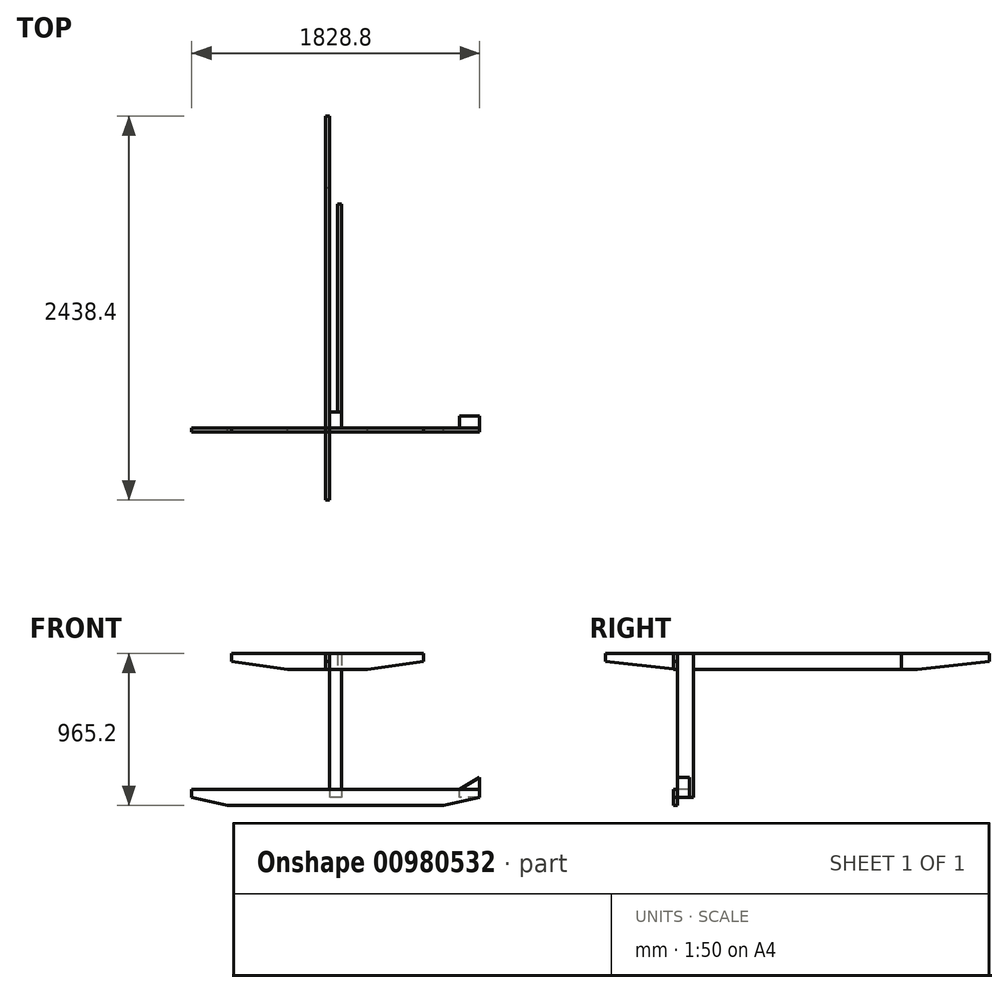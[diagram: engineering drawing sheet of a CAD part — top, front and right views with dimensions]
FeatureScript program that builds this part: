
annotation { "Feature Type Name" : "Feature", "Feature Type Description" : "" }
export const myFeature = defineFeature(function(context is Context, id is Id, definition is map)
    precondition{}
    {
        {
            var Q0;
            Q0=qCreatedBy(makeId("Right.planeOp"),FACE);
            var sketch = newSketch(context, id + "F0", { "sketchPlane" : qUnion([Q0])});
            skLineSegment(sketch, "E0.bottom", {"start": v(-1219.2, 50.8) * mm, "end": v(1219.2, 50.8) * mm});
            skLineSegment(sketch, "E0.left", {"start": v(-1219.2, 50.8) * mm, "end": v(-1219.2, 0) * mm});
            skLineSegment(sketch, "E0.right", {"start": v(1219.2, 50.8) * mm, "end": v(1219.2, 0) * mm});
            skLineSegment(sketch, "E1", {"start": v(-1219.2, -50.8) * mm, "end": v(1219.2, 50.8) * mm, "construction": true});
            skLineSegment(sketch, "E2", {"start": v(-1219.2, 0) * mm, "end": v(-762, -50.8) * mm});
            skLineSegment(sketch, "E3.MirrorCS", {"start": v(1219.2, 0) * mm, "end": v(762, -50.8) * mm});
            skLineSegment(sketch, "E4", {"start": v(762.5, -50.75) * mm, "end": v(762, -50.8) * mm});
            skLineSegment(sketch, "E5", {"start": v(-1219.2, 0) * mm, "end": v(-1219.2, -50.8) * mm});
            skLineSegment(sketch, "E6", {"start": v(-762, -50.8) * mm, "end": v(762, -50.8) * mm});
            skSolve(sketch);
        }
        {
            var Q0;
            Q0 = qSketchRegion(id + "F0", true);
            extrude(context, id + "F1", {"entities" : qUnion([Q0]), "endBound" : BoundingType.SYMMETRIC, "depth" : 25.4 * mm, "offsetDistance" : 25.4 * mm});
        }
        {
            var Q0;
            Q0=makeQuery(id+"F1.opExtrude","CAP_FACE",FACE,{"disambiguationData":[OSD([sQuery(id+"F0.wireOp",EDGE,"E0.bottom"),sQuery(id+"F0.wireOp",EDGE,"E0.left"),sQuery(id+"F0.wireOp",EDGE,"E0.right"),sQuery(id+"F0.wireOp",EDGE,"E2"),sQuery(id+"F0.wireOp",EDGE,"E3.MirrorCS"),sQuery(id+"F0.wireOp",EDGE,"E4"),sQuery(id+"F0.wireOp",EDGE,"E6")])],"isStart":false});
            var sketch = newSketch(context, id + "F2", { "sketchPlane" : qUnion([Q0])});
            skPoint(sketch, "E7", {"position": v(-762, 50.8) * mm});
            skLineSegment(sketch, "E8.bottom", {"start": v(-762, 50.8) * mm, "end": v(-660.4, 50.8) * mm});
            skLineSegment(sketch, "E8.top", {"start": v(-762, -863.6) * mm, "end": v(-660.4, -863.6) * mm});
            skLineSegment(sketch, "E8.left", {"start": v(-762, 50.8) * mm, "end": v(-762, -863.6) * mm});
            skLineSegment(sketch, "E8.right", {"start": v(-660.4, 50.8) * mm, "end": v(-660.4, -863.6) * mm});
            skSolve(sketch);
        }
        {
            var Q0;
            Q0 = qSketchRegion(id + "F2", true);
            extrude(context, id + "F3", {"entities" : qUnion([Q0]), "depth" : 76.2 * mm, "offsetDistance" : 25.4 * mm});
        }
        {
            var Q0;
            Q0=makeQuery(id+"F3.opExtrude","SWEPT_BODY",BODY,{"disambiguationData":[OSD([sQuery(id+"F2.wireOp",EDGE,"E8.bottom"),sQuery(id+"F2.wireOp",EDGE,"E8.top"),sQuery(id+"F2.wireOp",EDGE,"E8.left"),sQuery(id+"F2.wireOp",EDGE,"E8.right")])]});
            transform(context, id + "F4", {"entities" : qUnion([Q0]), "transformType" : TransformType.TRANSLATION_3D, "dx" : 0 * mm, "dy" : 1422.4 * mm, "dz" : 0 * mm, "makeCopy" : true});
        }
        {
            var Q0;
            Q0=makeQuery(id+"F3.opExtrude","SWEPT_FACE",FACE,{"disambiguationData":[OSD([sQuery(id+"F2.wireOp",EDGE,"E8.left")])]});
            var sketch = newSketch(context, id + "F5", { "sketchPlane" : qUnion([Q0])});
            skLineSegment(sketch, "E9.bottom", {"start": v(-609.6, 50.8) * mm, "end": v(609.6, 50.8) * mm});
            skLineSegment(sketch, "E9.top", {"start": v(-254, -50.8) * mm, "end": v(254, -50.8) * mm});
            skLineSegment(sketch, "E9.left", {"start": v(-609.6, 50.8) * mm, "end": v(-609.6, 0) * mm});
            skLineSegment(sketch, "E9.right", {"start": v(609.6, 50.8) * mm, "end": v(609.6, 0) * mm});
            skLineSegment(sketch, "E10", {"start": v(-609.6, 50.8) * mm, "end": v(609.6, -50.8) * mm, "construction": true});
            skLineSegment(sketch, "E11", {"start": v(-609.6, 0) * mm, "end": v(-254, -50.8) * mm});
            skPoint(sketch, "E12.orphan", {"position": v(-609.6, -50.8) * mm});
            skLineSegment(sketch, "E13.MirrorCS", {"start": v(609.6, 0) * mm, "end": v(254, -50.8) * mm});
            skSolve(sketch);
        }
        {
            var Q0;
            Q0 = qSketchRegion(id + "F5", true);
            extrude(context, id + "F6", {"entities" : qUnion([Q0]), "depth" : 25.4 * mm, "offsetDistance" : 25.4 * mm});
        }
        {
            var Q0;
            Q0=makeQuery(id+"F4.opPattern","COPY",BODY,{"derivedFrom":makeQuery(id+"F3.opExtrude","SWEPT_BODY",BODY,{"disambiguationData":[OSD([sQuery(id+"F2.wireOp",EDGE,"E8.bottom"),sQuery(id+"F2.wireOp",EDGE,"E8.top"),sQuery(id+"F2.wireOp",EDGE,"E8.left"),sQuery(id+"F2.wireOp",EDGE,"E8.right")])]}),"instanceName":"1"});
            deleteBodies(context, id + "F7", {"entities" : qUnion([Q0])});
        }
        {
            var Q0;
            Q0=makeQuery(id+"F3.opExtrude","SWEPT_FACE",FACE,{"disambiguationData":[OSD([sQuery(id+"F2.wireOp",EDGE,"E8.left")])]});
            var sketch = newSketch(context, id + "F8", { "sketchPlane" : qUnion([Q0])});
            skLineSegment(sketch, "E14.bottom", {"start": v(-863.6, -812.8) * mm, "end": v(965.2, -812.8) * mm});
            skLineSegment(sketch, "E14.top", {"start": v(-635, -914.4) * mm, "end": v(736.6, -914.4) * mm});
            skLineSegment(sketch, "E14.left", {"start": v(-863.6, -812.8) * mm, "end": v(-863.6, -863.6) * mm});
            skLineSegment(sketch, "E14.right", {"start": v(965.2, -812.8) * mm, "end": v(965.2, -863.6) * mm});
            skLineSegment(sketch, "E15", {"start": v(-863.6, -812.8) * mm, "end": v(965.2, -914.4) * mm, "construction": true});
            skLineSegment(sketch, "E16", {"start": v(-863.6, -863.6) * mm, "end": v(-635, -914.4) * mm});
            skPoint(sketch, "E17.orphan", {"position": v(-863.6, -914.4) * mm});
            skLineSegment(sketch, "E18.MirrorCS", {"start": v(965.2, -863.6) * mm, "end": v(736.6, -914.4) * mm});
            skSolve(sketch);
        }
        {
            var Q0;
            Q0 = qSketchRegion(id + "F8", true);
            extrude(context, id + "F9", {"entities" : qUnion([Q0]), "depth" : 25.4 * mm, "offsetDistance" : 25.4 * mm});
        }
        {
            var Q0;
            Q0=makeQuery(id+"F3.opExtrude","SWEPT_FACE",FACE,{"disambiguationData":[OSD([sQuery(id+"F2.wireOp",EDGE,"E8.right")])]});
            var sketch = newSketch(context, id + "F10", { "sketchPlane" : qUnion([Q0])});
            skLineSegment(sketch, "E19.bottom", {"start": v(-88.9, 50.8) * mm, "end": v(-63.5, 50.8) * mm});
            skLineSegment(sketch, "E19.top", {"start": v(-88.9, -50.8) * mm, "end": v(-63.5, -50.8) * mm});
            skLineSegment(sketch, "E19.left", {"start": v(-88.9, 50.8) * mm, "end": v(-88.9, -50.8) * mm});
            skLineSegment(sketch, "E19.right", {"start": v(-63.5, 50.8) * mm, "end": v(-63.5, -50.8) * mm});
            skSolve(sketch);
        }
        {
            var Q0;
            Q0 = qSketchRegion(id + "F10", true);
            extrude(context, id + "F11", {"entities" : qUnion([Q0]), "depth" : 1320.8 * mm, "offsetDistance" : 25.4 * mm});
        }
        {
            var Q0;
            Q0=makeQuery(id+"F9.opExtrude","CAP_FACE",FACE,{"disambiguationData":[OSD([sQuery(id+"F8.wireOp",EDGE,"E14.bottom"),sQuery(id+"F8.wireOp",EDGE,"E14.top"),sQuery(id+"F8.wireOp",EDGE,"E14.left"),sQuery(id+"F8.wireOp",EDGE,"E14.right"),sQuery(id+"F8.wireOp",EDGE,"E16"),sQuery(id+"F8.wireOp",EDGE,"E18.MirrorCS")])],"isStart":true});
            var sketch = newSketch(context, id + "F12", { "sketchPlane" : qUnion([Q0])});
            skLineSegment(sketch, "E20.1", {"start": v(-965.2, -812.8) * mm, "end": v(-965.2, -863.6) * mm});
            skLineSegment(sketch, "E21", {"start": v(-965.2, -863.6) * mm, "end": v(-838.2, -863.6) * mm});
            skLineSegment(sketch, "E22", {"start": v(-838.2, -863.6) * mm, "end": v(-838.2, -812.8) * mm});
            skLineSegment(sketch, "E23", {"start": v(-838.2, -812.8) * mm, "end": v(-965.2, -736.6) * mm});
            skLineSegment(sketch, "E24", {"start": v(-965.2, -736.6) * mm, "end": v(-965.2, -812.8) * mm});
            skPoint(sketch, "E25.orphan", {"position": v(863.6, -812.8) * mm});
            skSolve(sketch);
        }
        {
            var Q0;
            Q0 = qSketchRegion(id + "F12", true);
            extrude(context, id + "F13", {"entities" : qUnion([Q0]), "depth" : 76.2 * mm, "offsetDistance" : 25.4 * mm});
        }
    });
